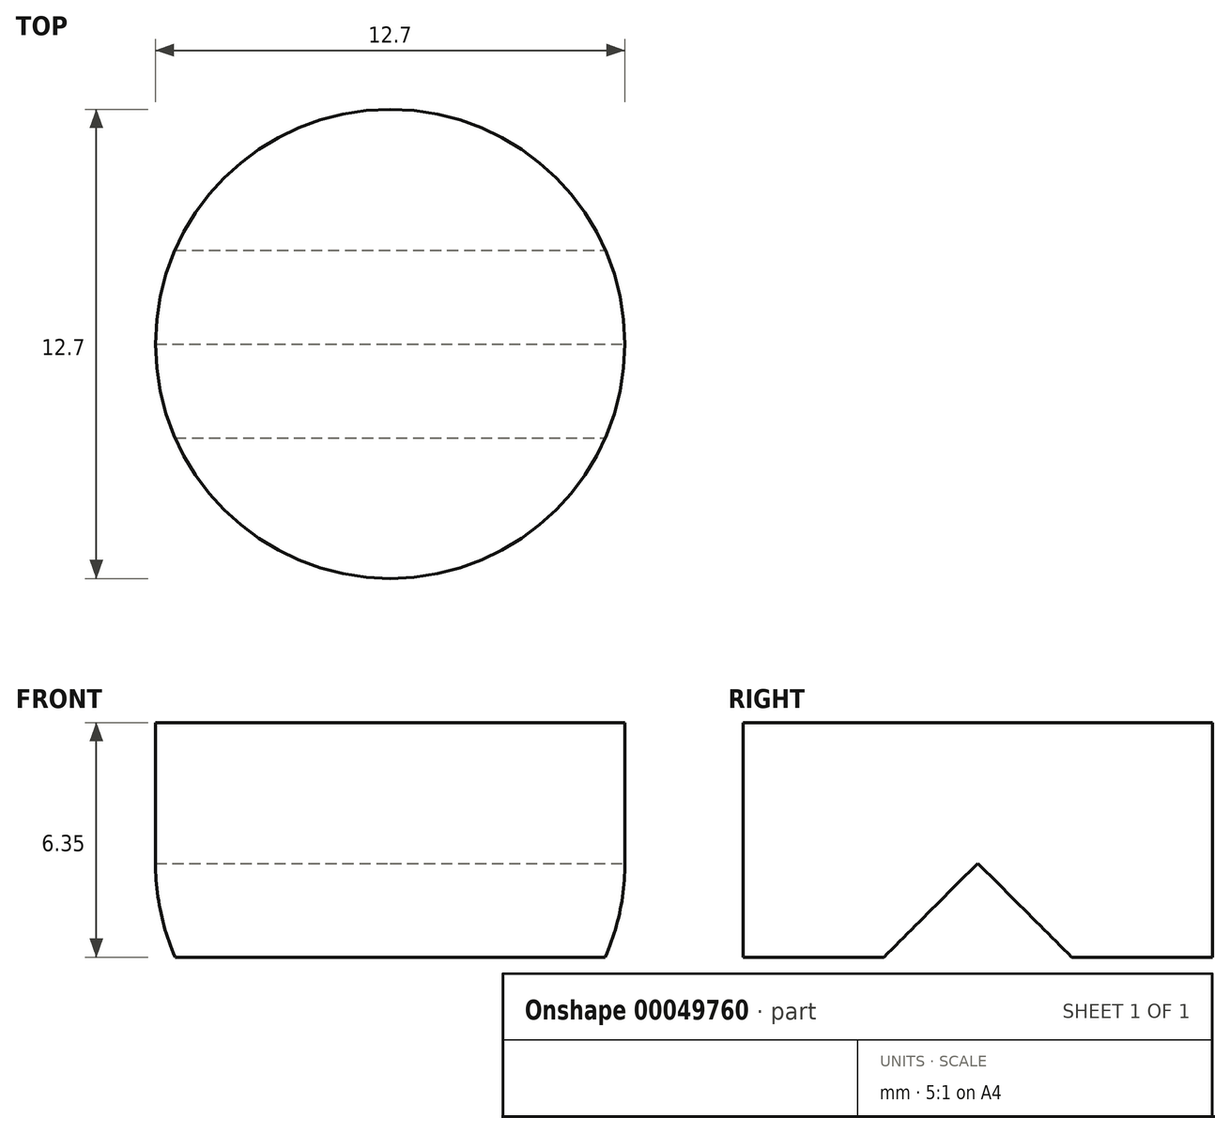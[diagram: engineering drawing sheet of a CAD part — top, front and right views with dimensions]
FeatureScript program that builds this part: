
annotation { "Feature Type Name" : "Feature", "Feature Type Description" : "" }
export const myFeature = defineFeature(function(context is Context, id is Id, definition is map)
    precondition{}
    {
        {
            var Q0;
            Q0=qCreatedBy(makeId("Top.planeOp"),FACE);
            var sketch = newSketch(context, id + "F0", { "sketchPlane" : qUnion([Q0])});
            skCircle(sketch, "E0", {"center": v(0, 0) * mm, "radius": 6.35 * mm});
            skSolve(sketch);
        }
        {
            var Q0;
            Q0=qSketchRegion(id+"F0",true);
            extrude(context, id + "F1", {"entities" : qUnion([Q0]), "depth" : 6.35 * mm});
        }
        {
            var Q0;
            Q0=qCreatedBy(makeId("Top.planeOp"),FACE);
            var sketch = newSketch(context, id + "F2", { "sketchPlane" : qUnion([Q0])});
            skCircle(sketch, "E1", {"center": v(0, 0) * mm, "radius": 1.27 * mm});
            skSolve(sketch);
        }
        {
            var Q0;
            Q0=makeQuery(id+"F2.imprint","IMPRINT",FACE,{"disambiguationData":[TD([[makeQuery(id+"F2.imprint","IMPRINT",EDGE,{"derivedFrom":sQuery(id+"F2.wireOp",EDGE,"E1")}),1.0]])]});
            cPlane(context, id + "F3", {"entities" : qUnion([Q0]), "cplaneType" : CPlaneType.OFFSET, "offset" : 2.54 * mm, "width" : 152.4 * mm, "height" : 152.4 * mm});
        }
        {
            var Q0;
            Q0=qCreatedBy(id+"F3.planeOp",FACE);
            var sketch = newSketch(context, id + "F4", { "sketchPlane" : qUnion([Q0])});
            skPoint(sketch, "E2", {"position": v(0, 0) * mm});
            skSolve(sketch);
        }
        {
            var Q0;
            Q0=sQuery(id+"F4.wireOp",VERTEX,"E2");
            var Q1;
            Q1=makeQuery(id+"F2.imprint","IMPRINT",FACE,{"disambiguationData":[TD([[makeQuery(id+"F2.imprint","IMPRINT",EDGE,{"derivedFrom":sQuery(id+"F2.wireOp",EDGE,"E1")}),1.0]])]});
            loft(context, id + "F5", {"operationType" : NewBodyOperationType.REMOVE, "sheetProfilesArray" : [{ "sheetProfileEntities" : qUnion([Q0]) }, { "sheetProfileEntities" : qUnion([Q1]) }]});
        }
        {
            var Q0;
            Q0=qCreatedBy(makeId("Right.planeOp"),FACE);
            var sketch = newSketch(context, id + "F6", { "sketchPlane" : qUnion([Q0])});
            skCircle(sketch, "E3.cCircle", {"center": v(0, 0) * mm, "radius": 2.54 * mm, "construction": true});
            skLineSegment(sketch, "E3.0", {"start": v(2.54, 0) * mm, "end": v(0, -2.54) * mm});
            skLineSegment(sketch, "E3.1", {"start": v(0, -2.54) * mm, "end": v(-2.54, 0) * mm});
            skLineSegment(sketch, "E3.2", {"start": v(-2.54, 0) * mm, "end": v(0, 2.54) * mm});
            skLineSegment(sketch, "E3.3", {"start": v(0, 2.54) * mm, "end": v(2.54, 0) * mm});
            skSolve(sketch);
        }
        {
            var Q0;
            Q0 = qSketchRegion(id + "F6", true);
            extrude(context, id + "F7", {"entities" : qUnion([Q0]), "operationType" : NewBodyOperationType.REMOVE, "endBound" : BoundingType.SYMMETRIC, "oppositeDirection" : true, "depth" : 25.4 * mm});
        }
    });
